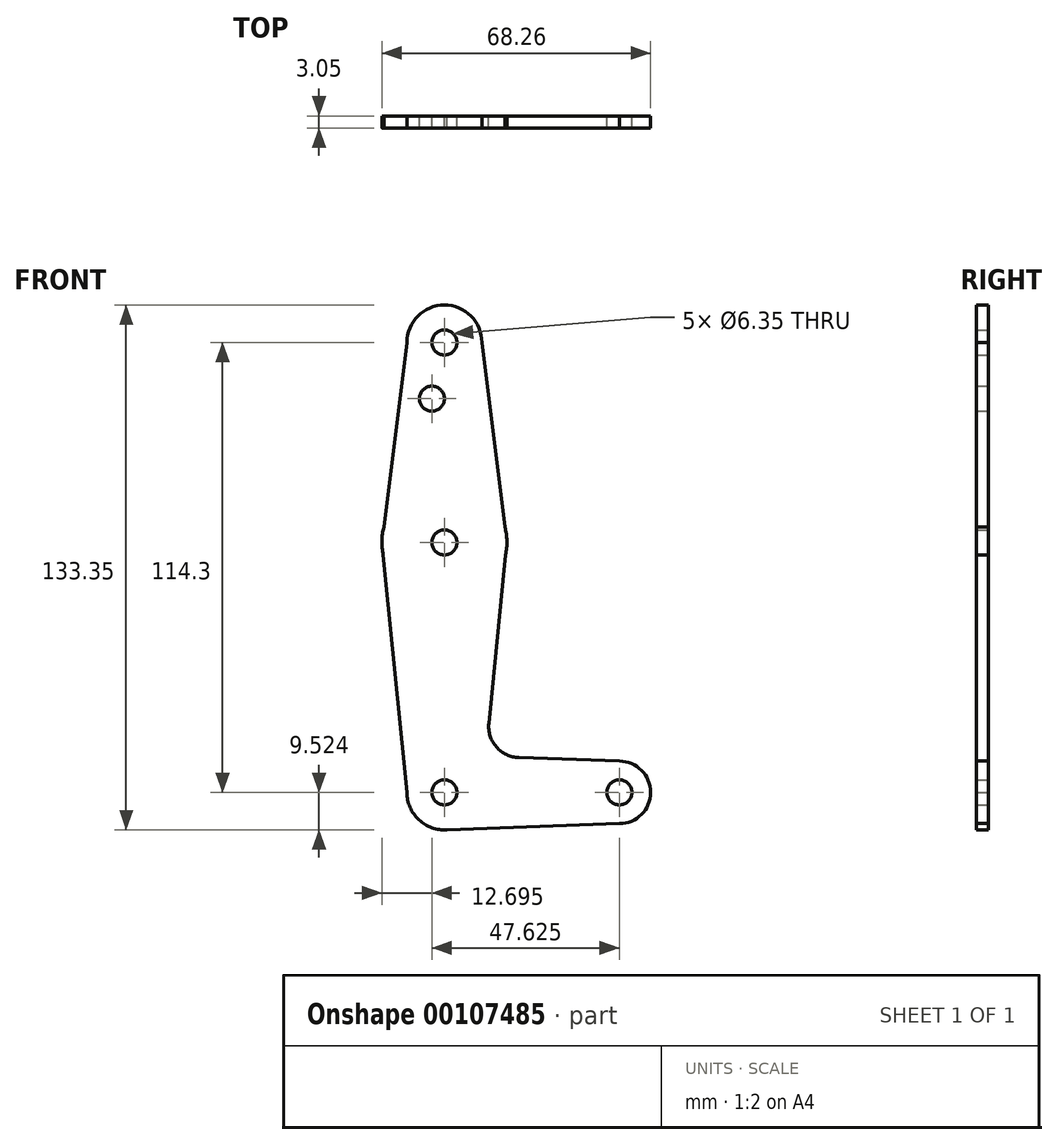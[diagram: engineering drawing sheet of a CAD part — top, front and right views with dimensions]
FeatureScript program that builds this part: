
annotation { "Feature Type Name" : "Feature", "Feature Type Description" : "" }
export const myFeature = defineFeature(function(context is Context, id is Id, definition is map)
    precondition{}
    {
        {
            var Q0;
            Q0=qCreatedBy(makeId("Front.planeOp"),FACE);
            var sketch = newSketch(context, id + "F0", { "sketchPlane" : qUnion([Q0])});
            skLineSegment(sketch, "E0", {"start": v(0, 69.4) * mm, "end": v(0, -44.9) * mm, "construction": true});
            skLineSegment(sketch, "E1", {"start": v(0, -44.9) * mm, "end": v(44.45, -44.9) * mm, "construction": true});
            skCircle(sketch, "E2", {"center": v(0, 69.4) * mm, "radius": 9.53 * mm});
            skCircle(sketch, "E3", {"center": v(0, 18.6) * mm, "radius": 15.88 * mm});
            skCircle(sketch, "E4", {"center": v(0, -44.9) * mm, "radius": 9.52 * mm});
            skCircle(sketch, "E5", {"center": v(44.45, -44.9) * mm, "radius": 7.94 * mm});
            skLineSegment(sketch, "E6", {"start": v(-9.52, 69.4) * mm, "end": v(-15.87, 18.6) * mm});
            skLineSegment(sketch, "E7", {"start": v(-15.87, 18.6) * mm, "end": v(-9.52, -44.9) * mm});
            skLineSegment(sketch, "E8", {"start": v(9.52, 69.4) * mm, "end": v(15.88, 18.6) * mm});
            skLineSegment(sketch, "E9", {"start": v(15.88, 18.6) * mm, "end": v(11.28, -27.31) * mm});
            skLineSegment(sketch, "E10", {"start": v(18.9, -36.05) * mm, "end": v(44.45, -36.96) * mm});
            skLineSegment(sketch, "E11", {"start": v(0, -54.42) * mm, "end": v(44.45, -52.83) * mm});
            skCircle(sketch, "E12", {"center": v(0, 69.4) * mm, "radius": 3.18 * mm});
            skCircle(sketch, "E13", {"center": v(0, 18.6) * mm, "radius": 3.18 * mm});
            skCircle(sketch, "E14", {"center": v(0, -44.9) * mm, "radius": 3.18 * mm});
            skCircle(sketch, "E15", {"center": v(44.45, -44.9) * mm, "radius": 3.18 * mm});
            skCircle(sketch, "E16", {"center": v(-3.17, 55.13) * mm, "radius": 3.18 * mm});
            skArc(sketch, "E17.filletArc", {"start": v(11.28, -27.31) * mm, "mid": v(13.2, -33.33) * mm, "end": v(18.9, -36.05) * mm});
            skSolve(sketch);
        }
        {
            var Q0;
            Q0 = qSketchRegion(id + "F0", true);
            extrude(context, id + "F1", {"entities" : qUnion([Q0]), "depth" : 3.05 * mm});
        }
    });
